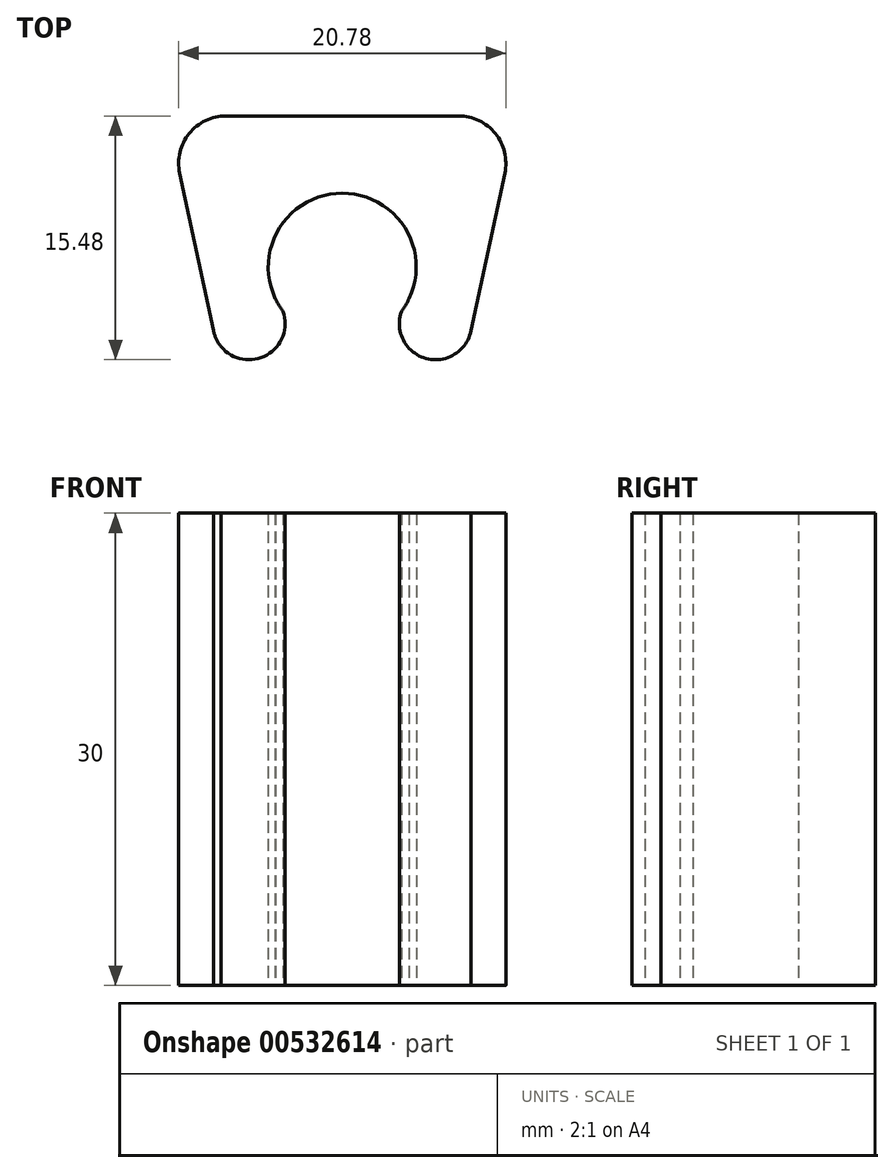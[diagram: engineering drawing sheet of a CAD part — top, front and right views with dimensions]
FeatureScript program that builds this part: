
annotation { "Feature Type Name" : "Feature", "Feature Type Description" : "" }
export const myFeature = defineFeature(function(context is Context, id is Id, definition is map)
    precondition{}
    {
        {
            var Q0;
            Q0=qCreatedBy(makeId("Top.planeOp"),FACE);
            var sketch = newSketch(context, id + "F0", { "sketchPlane" : qUnion([Q0])});
            skLineSegment(sketch, "E0", {"start": v(8.18, -5.93) * mm, "end": v(10.32, 4.07) * mm});
            skLineSegment(sketch, "E1", {"start": v(7.39, 7.7) * mm, "end": v(-7.39, 7.7) * mm});
            skArc(sketch, "E2", {"start": v(4.25, -3.9) * mm, "mid": v(0, 2.8) * mm, "end": v(-4.25, -3.9) * mm});
            skLineSegment(sketch, "E3", {"start": v(4.93, 7.7) * mm, "end": v(4.93, -3.9) * mm, "construction": true});
            skLineSegment(sketch, "E4.MirrorCS", {"start": v(-8.16, -6) * mm, "end": v(-10.32, 4.07) * mm});
            skPoint(sketch, "E5.visualSharp", {"position": v(11.1, 7.7) * mm});
            skArc(sketch, "E5.filletArc", {"start": v(10.32, 4.07) * mm, "mid": v(9.72, 6.59) * mm, "end": v(7.39, 7.7) * mm});
            skPoint(sketch, "E6.visualSharp", {"position": v(-11.1, 7.7) * mm});
            skArc(sketch, "E6.filletArc", {"start": v(-7.39, 7.7) * mm, "mid": v(-9.72, 6.59) * mm, "end": v(-10.32, 4.07) * mm});
            skArc(sketch, "E7.filletArc", {"start": v(-8.16, -6) * mm, "mid": v(-7.99, -6.5) * mm, "end": v(-7.69, -6.96) * mm});
            skArc(sketch, "E8", {"start": v(-8.18, -5.93) * mm, "mid": v(-5.32, -7.7) * mm, "end": v(-3.75, -4.72) * mm});
            skArc(sketch, "E9.MirrorCS", {"start": v(8.18, -5.93) * mm, "mid": v(5.32, -7.7) * mm, "end": v(3.75, -4.72) * mm});
            skArc(sketch, "E10", {"start": v(-4.24, -3.91) * mm, "mid": v(-4.02, -4.33) * mm, "end": v(-3.75, -4.72) * mm});
            skArc(sketch, "E11.trimOffspring", {"start": v(-4.24, -3.91) * mm, "mid": v(-4.25, -3.9) * mm, "end": v(-4.25, -3.9) * mm});
            skArc(sketch, "E12.trimOffspring", {"start": v(4.24, -3.91) * mm, "mid": v(4.25, -3.9) * mm, "end": v(4.25, -3.9) * mm});
            skArc(sketch, "E13.trimOffspring", {"start": v(3.75, -4.72) * mm, "mid": v(4.02, -4.33) * mm, "end": v(4.24, -3.91) * mm});
            skSolve(sketch);
        }
        {
            var Q0;
            Q0 = qSketchRegion(id + "F0", true);
            extrude(context, id + "F1", {"entities" : qUnion([Q0]), "depth" : 30 * mm, "offsetDistance" : 25 * mm});
        }
    });
